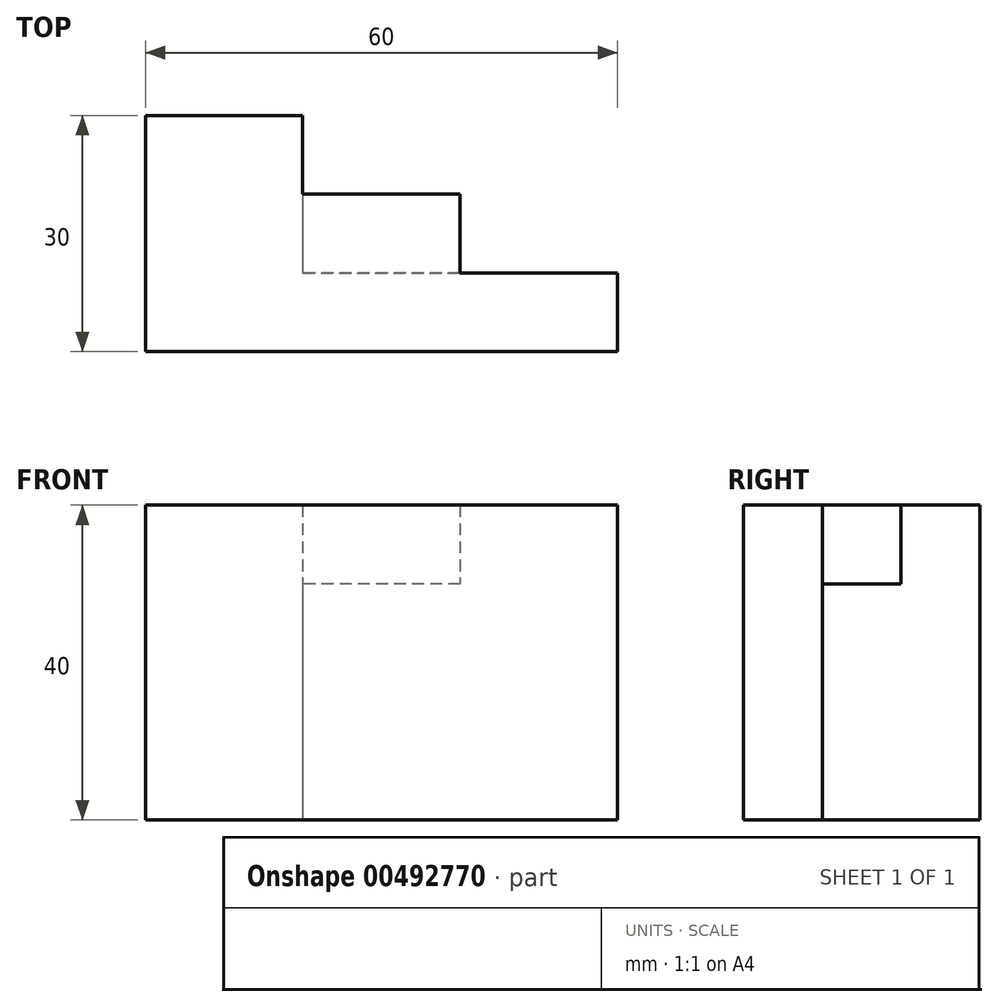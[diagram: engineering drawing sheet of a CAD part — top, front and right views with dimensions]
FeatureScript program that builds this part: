
annotation { "Feature Type Name" : "Feature", "Feature Type Description" : "" }
export const myFeature = defineFeature(function(context is Context, id is Id, definition is map)
    precondition{}
    {
        {
            var Q0;
            Q0=qCreatedBy(makeId("Top.planeOp"),FACE);
            var sketch = newSketch(context, id + "F0", { "sketchPlane" : qUnion([Q0])});
            skLineSegment(sketch, "E0", {"start": v(0, 0) * mm, "end": v(0, 30) * mm});
            skLineSegment(sketch, "E1", {"start": v(0, 30) * mm, "end": v(20, 30) * mm});
            skLineSegment(sketch, "E2", {"start": v(20, 30) * mm, "end": v(20, 10) * mm});
            skLineSegment(sketch, "E3", {"start": v(20, 10) * mm, "end": v(60, 10) * mm});
            skLineSegment(sketch, "E4", {"start": v(60, 10) * mm, "end": v(60, 0) * mm});
            skLineSegment(sketch, "E5", {"start": v(60, 0) * mm, "end": v(0, 0) * mm});
            skSolve(sketch);
        }
        {
            var Q0;
            Q0=makeQuery(id+"F0.imprint","IMPRINT",FACE,{"disambiguationData":[TD([[makeQuery(id+"F0.imprint","IMPRINT",EDGE,{"derivedFrom":sQuery(id+"F0.wireOp",EDGE,"E0")}),-1.0]])]});
            extrude(context, id + "F1", {"entities" : qUnion([Q0]), "depth" : 40 * mm});
        }
        {
            var Q0;
            Q0=makeQuery(id+"F1.opExtrude","SWEPT_FACE",FACE,{"disambiguationData":[OSD([sQuery(id+"F0.wireOp",EDGE,"E3")])]});
            var sketch = newSketch(context, id + "F2", { "sketchPlane" : qUnion([Q0])});
            skLineSegment(sketch, "E6", {"start": v(-20, 40) * mm, "end": v(-40, 40) * mm});
            skLineSegment(sketch, "E7", {"start": v(-40, 40) * mm, "end": v(-40, 30) * mm});
            skLineSegment(sketch, "E8", {"start": v(-40, 30) * mm, "end": v(-20, 30) * mm});
            skSolve(sketch);
        }
        {
            var Q0;
            {var subQ0=sQuery(id+"F2.wireOp",EDGE,"E6");Q0=makeQuery(id+"F2.imprint","IMPRINT",FACE,{"disambiguationData":[TD([[makeQuery(id+"F2.imprint","IMPRINT",EDGE,{"derivedFrom":subQ0}),1.0]])]});}
            extrude(context, id + "F3", {"entities" : qUnion([Q0]), "operationType" : NewBodyOperationType.ADD, "depth" : 10 * mm});
        }
    });
